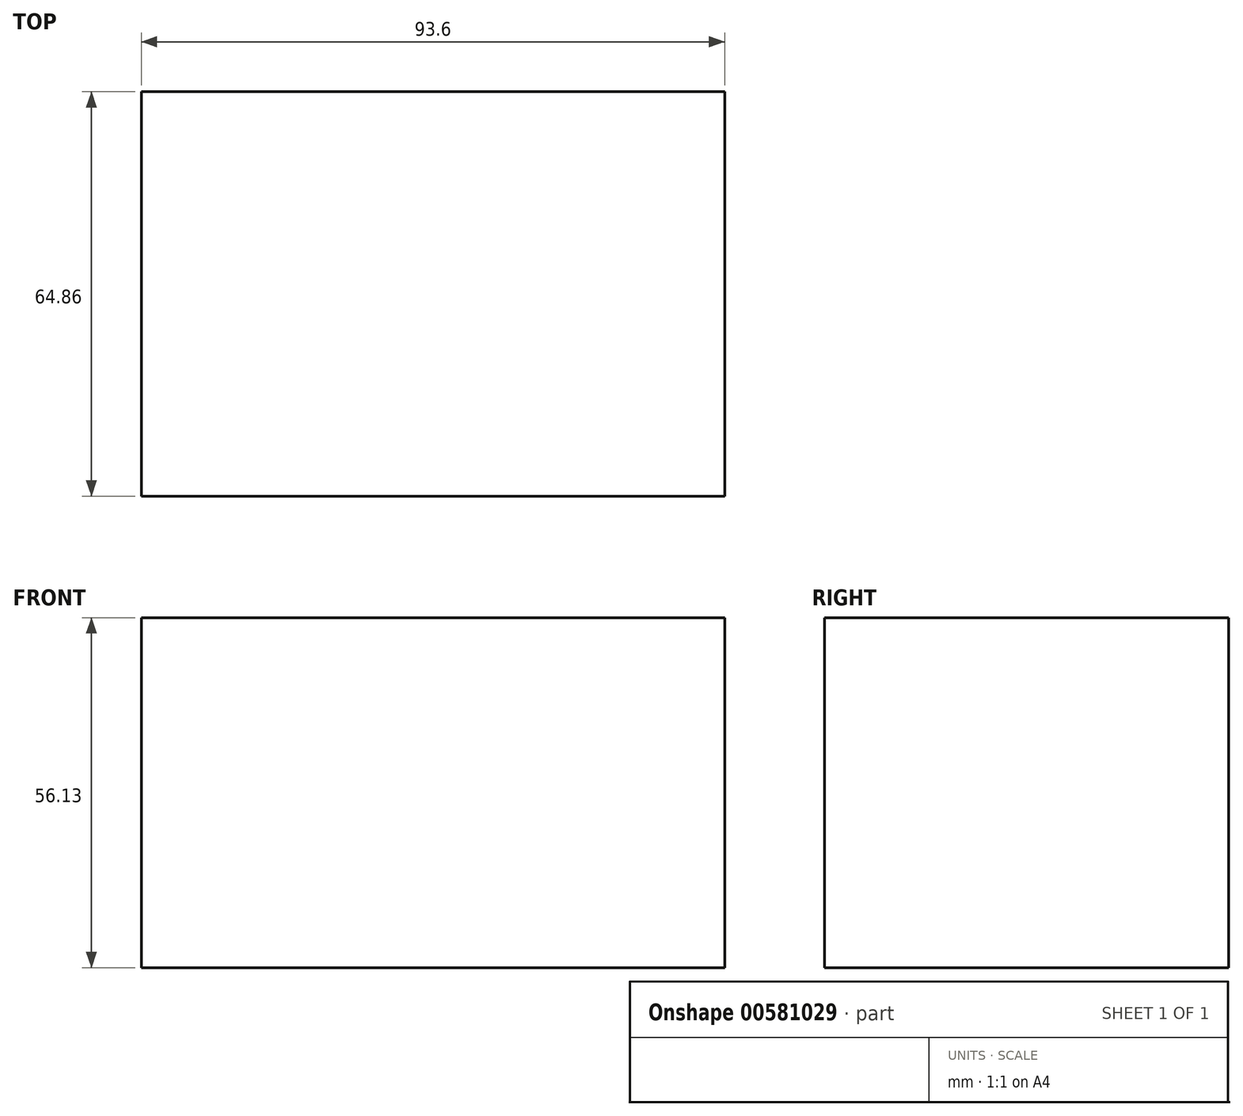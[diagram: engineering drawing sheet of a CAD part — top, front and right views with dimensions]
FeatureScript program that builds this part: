
annotation { "Feature Type Name" : "Feature", "Feature Type Description" : "" }
export const myFeature = defineFeature(function(context is Context, id is Id, definition is map)
    precondition{}
    {
        {
            var Q0;
            Q0=qCreatedBy(makeId("Top.planeOp"),FACE);
            var sketch = newSketch(context, id + "F0", { "sketchPlane" : qUnion([Q0])});
            skLineSegment(sketch, "E0.bottom", {"start": v(-46.8, -32.43) * mm, "end": v(46.8, -32.43) * mm});
            skLineSegment(sketch, "E0.top", {"start": v(-46.8, 32.43) * mm, "end": v(46.8, 32.43) * mm});
            skLineSegment(sketch, "E0.left", {"start": v(-46.8, -32.43) * mm, "end": v(-46.8, 32.43) * mm});
            skLineSegment(sketch, "E0.right", {"start": v(46.8, -32.43) * mm, "end": v(46.8, 32.43) * mm});
            skPoint(sketch, "E0.middle", {"position": v(0, 0) * mm});
            skSolve(sketch);
        }
        {
            var Q0;
            Q0 = qSketchRegion(id + "F0", true);
            extrude(context, id + "F1", {"entities" : qUnion([Q0]), "oppositeDirection" : true, "depth" : 56.13 * mm, "offsetDistance" : 25.4 * mm});
        }
    });
